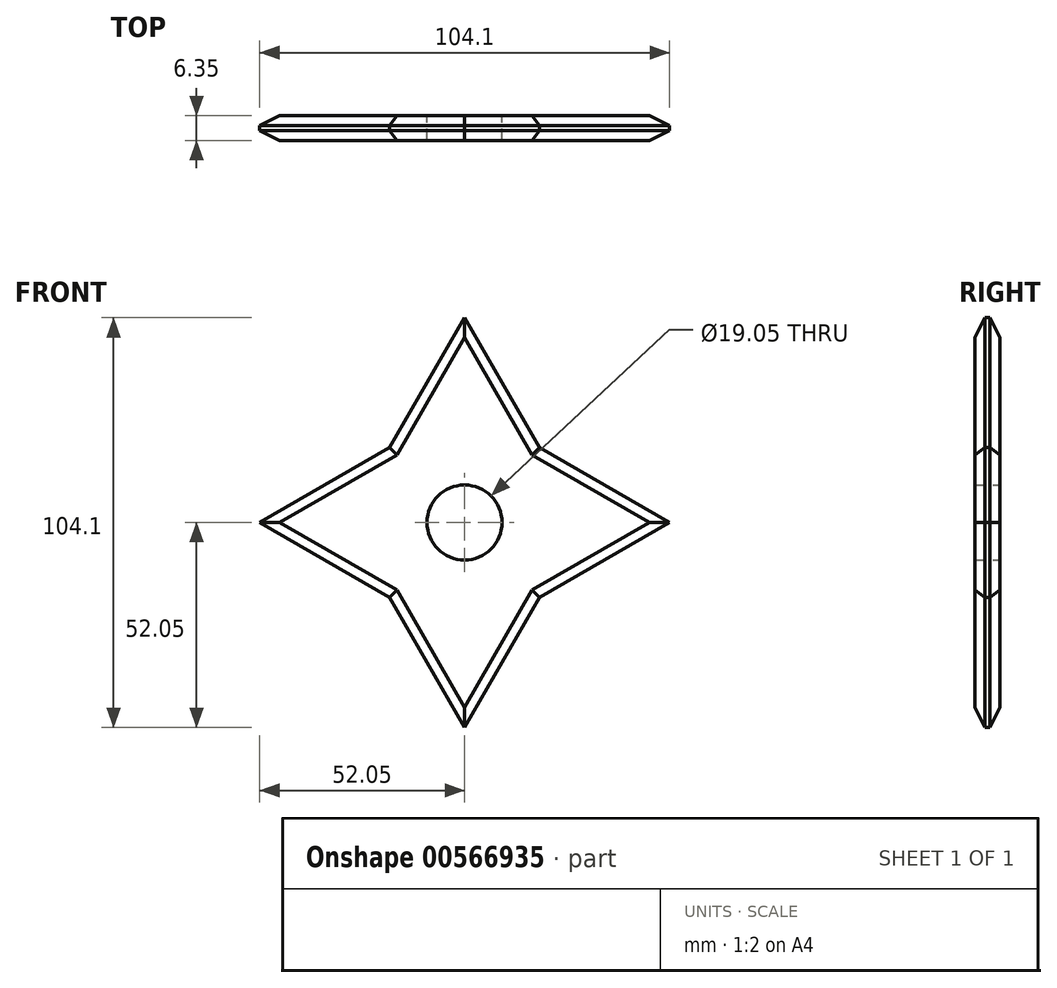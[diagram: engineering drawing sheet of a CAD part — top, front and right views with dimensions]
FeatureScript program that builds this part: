
annotation { "Feature Type Name" : "Feature", "Feature Type Description" : "" }
export const myFeature = defineFeature(function(context is Context, id is Id, definition is map)
    precondition{}
    {
        {
            var Q0;
            Q0=qCreatedBy(makeId("Front.planeOp"),FACE);
            var sketch = newSketch(context, id + "F0", { "sketchPlane" : qUnion([Q0])});
            skLineSegment(sketch, "E0.bottom", {"start": v(0, 0) * mm, "end": v(38.1, 0) * mm});
            skLineSegment(sketch, "E0.top", {"start": v(0, 38.1) * mm, "end": v(38.1, 38.1) * mm});
            skLineSegment(sketch, "E0.left", {"start": v(0, 0) * mm, "end": v(0, 38.1) * mm});
            skLineSegment(sketch, "E0.right", {"start": v(38.1, 0) * mm, "end": v(38.1, 38.1) * mm});
            skLineSegment(sketch, "E1", {"start": v(0, 38.1) * mm, "end": v(19.05, 71.1) * mm});
            skLineSegment(sketch, "E2", {"start": v(19.05, 71.1) * mm, "end": v(38.1, 38.1) * mm});
            skLineSegment(sketch, "E3", {"start": v(0, 38.1) * mm, "end": v(-33, 19.05) * mm});
            skPoint(sketch, "E3.endSnap0", {"position": v(0, 19.05) * mm});
            skLineSegment(sketch, "E4", {"start": v(-33, 19.05) * mm, "end": v(0, 0) * mm});
            skLineSegment(sketch, "E5", {"start": v(0, 0) * mm, "end": v(19.05, -33) * mm});
            skLineSegment(sketch, "E6", {"start": v(19.05, -33) * mm, "end": v(38.1, 0) * mm});
            skLineSegment(sketch, "E7", {"start": v(38.1, 38.1) * mm, "end": v(71.1, 19.05) * mm});
            skLineSegment(sketch, "E8", {"start": v(71.1, 19.05) * mm, "end": v(38.1, 0) * mm});
            skCircle(sketch, "E9", {"center": v(19.05, 19.05) * mm, "radius": 9.53 * mm});
            skSolve(sketch);
        }
        {
            var Q0;
            Q0=makeQuery(id+"F0.imprint","IMPRINT",FACE,{"disambiguationData":[TD([[makeQuery(id+"F0.imprint","IMPRINT",EDGE,{"derivedFrom":sQuery(id+"F0.wireOp",EDGE,"E0.bottom")}),1.0]])]});
            var Q1;
            Q1=makeQuery(id+"F0.imprint","IMPRINT",FACE,{"disambiguationData":[TD([[makeQuery(id+"F0.imprint","IMPRINT",EDGE,{"derivedFrom":sQuery(id+"F0.wireOp",EDGE,"E0.top")}),1.0]])]});
            var Q2;
            Q2=makeQuery(id+"F0.imprint","IMPRINT",FACE,{"disambiguationData":[TD([[makeQuery(id+"F0.imprint","IMPRINT",EDGE,{"derivedFrom":sQuery(id+"F0.wireOp",EDGE,"E0.left")}),1.0]])]});
            var Q3;
            Q3=makeQuery(id+"F0.imprint","IMPRINT",FACE,{"disambiguationData":[TD([[makeQuery(id+"F0.imprint","IMPRINT",EDGE,{"derivedFrom":sQuery(id+"F0.wireOp",EDGE,"E0.right")}),-1.0]])]});
            var Q4;
            Q4=makeQuery(id+"F0.imprint","IMPRINT",FACE,{"disambiguationData":[TD([[makeQuery(id+"F0.imprint","IMPRINT",EDGE,{"derivedFrom":sQuery(id+"F0.wireOp",EDGE,"E0.bottom")}),-1.0]])]});
            extrude(context, id + "F1", {"entities" : qUnion([Q0, Q1, Q2, Q3, Q4]), "depth" : 6.35 * mm});
        }
        {
            var Q0;
            Q0=makeQuery(id+"F1.opExtrude","CAP_EDGE",EDGE,{"disambiguationData":[OSD([sQuery(id+"F0.wireOp",EDGE,"E1")])],"isStart":false});
            var Q1;
            Q1=makeQuery(id+"F1.opExtrude","CAP_EDGE",EDGE,{"disambiguationData":[OSD([sQuery(id+"F0.wireOp",EDGE,"E3")])],"isStart":false});
            var Q2;
            Q2=makeQuery(id+"F1.opExtrude","CAP_EDGE",EDGE,{"disambiguationData":[OSD([sQuery(id+"F0.wireOp",EDGE,"E4")])],"isStart":false});
            var Q3;
            Q3=makeQuery(id+"F1.opExtrude","CAP_EDGE",EDGE,{"disambiguationData":[OSD([sQuery(id+"F0.wireOp",EDGE,"E5")])],"isStart":false});
            var Q4;
            Q4=makeQuery(id+"F1.opExtrude","CAP_EDGE",EDGE,{"disambiguationData":[OSD([sQuery(id+"F0.wireOp",EDGE,"E6")])],"isStart":false});
            var Q5;
            Q5=makeQuery(id+"F1.opExtrude","CAP_EDGE",EDGE,{"disambiguationData":[OSD([sQuery(id+"F0.wireOp",EDGE,"E8")])],"isStart":false});
            var Q6;
            Q6=makeQuery(id+"F1.opExtrude","CAP_EDGE",EDGE,{"disambiguationData":[OSD([sQuery(id+"F0.wireOp",EDGE,"E7")])],"isStart":false});
            var Q7;
            Q7=makeQuery(id+"F1.opExtrude","CAP_EDGE",EDGE,{"disambiguationData":[OSD([sQuery(id+"F0.wireOp",EDGE,"E2")])],"isStart":false});
            chamfer(context, id + "F2", {"entities" : qUnion([Q0, Q1, Q2, Q3, Q4, Q5, Q6, Q7]), "width" : 2.54 * mm, "tangentPropagation" : true});
        }
        {
            var Q0;
            Q0=makeQuery(id+"F1.opExtrude","CAP_EDGE",EDGE,{"disambiguationData":[OSD([sQuery(id+"F0.wireOp",EDGE,"E5")])],"isStart":true});
            var Q1;
            Q1=makeQuery(id+"F1.opExtrude","CAP_EDGE",EDGE,{"disambiguationData":[OSD([sQuery(id+"F0.wireOp",EDGE,"E6")])],"isStart":true});
            var Q2;
            Q2=makeQuery(id+"F1.opExtrude","CAP_EDGE",EDGE,{"disambiguationData":[OSD([sQuery(id+"F0.wireOp",EDGE,"E8")])],"isStart":true});
            var Q3;
            Q3=makeQuery(id+"F1.opExtrude","CAP_EDGE",EDGE,{"disambiguationData":[OSD([sQuery(id+"F0.wireOp",EDGE,"E7")])],"isStart":true});
            var Q4;
            Q4=makeQuery(id+"F1.opExtrude","CAP_EDGE",EDGE,{"disambiguationData":[OSD([sQuery(id+"F0.wireOp",EDGE,"E2")])],"isStart":true});
            var Q5;
            Q5=makeQuery(id+"F1.opExtrude","CAP_EDGE",EDGE,{"disambiguationData":[OSD([sQuery(id+"F0.wireOp",EDGE,"E1")])],"isStart":true});
            var Q6;
            Q6=makeQuery(id+"F1.opExtrude","CAP_EDGE",EDGE,{"disambiguationData":[OSD([sQuery(id+"F0.wireOp",EDGE,"E3")])],"isStart":true});
            var Q7;
            Q7=makeQuery(id+"F1.opExtrude","CAP_EDGE",EDGE,{"disambiguationData":[OSD([sQuery(id+"F0.wireOp",EDGE,"E4")])],"isStart":true});
            chamfer(context, id + "F3", {"entities" : qUnion([Q0, Q1, Q2, Q3, Q4, Q5, Q6, Q7]), "width" : 2.54 * mm, "tangentPropagation" : true});
        }
    });
